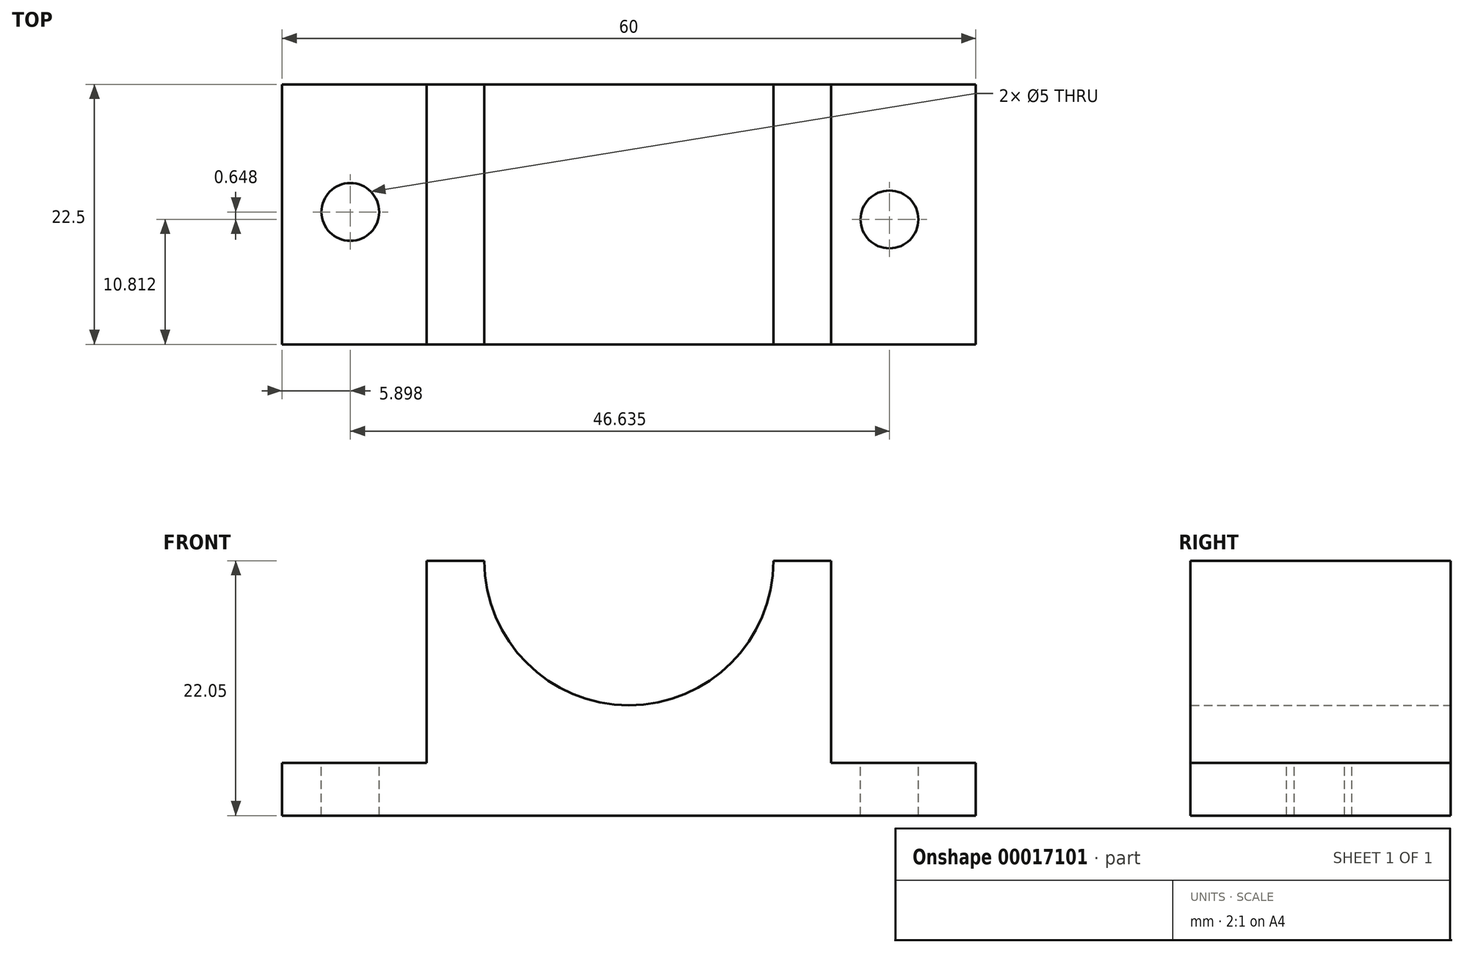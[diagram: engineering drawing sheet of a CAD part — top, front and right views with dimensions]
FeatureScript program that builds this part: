
annotation { "Feature Type Name" : "Feature", "Feature Type Description" : "" }
export const myFeature = defineFeature(function(context is Context, id is Id, definition is map)
    precondition{}
    {
        {
            var Q0;
            Q0=qCreatedBy(makeId("Front.planeOp"),FACE);
            var sketch = newSketch(context, id + "F0", { "sketchPlane" : qUnion([Q0])});
            skLineSegment(sketch, "E0", {"start": v(-1.56, 17.5) * mm, "end": v(-6.56, 17.5) * mm});
            skLineSegment(sketch, "E1", {"start": v(-6.56, 17.5) * mm, "end": v(-6.56, 0) * mm});
            skLineSegment(sketch, "E2", {"start": v(-6.56, 0) * mm, "end": v(-19.06, 0) * mm});
            skLineSegment(sketch, "E3", {"start": v(-19.06, 0) * mm, "end": v(-19.06, -4.55) * mm});
            skLineSegment(sketch, "E4", {"start": v(-19.06, -4.55) * mm, "end": v(40.94, -4.55) * mm});
            skLineSegment(sketch, "E5", {"start": v(40.94, -4.55) * mm, "end": v(40.94, 0) * mm});
            skLineSegment(sketch, "E6", {"start": v(40.94, 0) * mm, "end": v(28.44, 0) * mm});
            skLineSegment(sketch, "E7", {"start": v(28.44, 0) * mm, "end": v(28.44, 17.5) * mm});
            skLineSegment(sketch, "E8", {"start": v(28.44, 17.5) * mm, "end": v(23.44, 17.5) * mm});
            skArc(sketch, "E9", {"start": v(-1.56, 17.5) * mm, "mid": v(10.94, 5) * mm, "end": v(23.44, 17.5) * mm});
            skSolve(sketch);
        }
        {
            var Q0;
            Q0=makeQuery(id+"F0.imprint","IMPRINT",FACE,{"disambiguationData":[TD([[makeQuery(id+"F0.imprint","IMPRINT",EDGE,{"derivedFrom":sQuery(id+"F0.wireOp",EDGE,"E0")}),1.0]])]});
            extrude(context, id + "F1", {"entities" : qUnion([Q0]), "depth" : 22.5 * mm});
        }
        {
            var Q0;
            Q0=qCreatedBy(makeId("Top.planeOp"),FACE);
            var sketch = newSketch(context, id + "F2", { "sketchPlane" : qUnion([Q0])});
            skCircle(sketch, "E10", {"center": v(-13.16, -11.04) * mm, "radius": 2.5 * mm});
            skSolve(sketch);
        }
        {
            var Q0;
            Q0=qCreatedBy(makeId("Top.planeOp"),FACE);
            var sketch = newSketch(context, id + "F3", { "sketchPlane" : qUnion([Q0])});
            skCircle(sketch, "E11", {"center": v(33.47, -11.69) * mm, "radius": 2.5 * mm});
            skSolve(sketch);
        }
        {
            var Q0;
            Q0=sQuery(id+"F3.wireOp",VERTEX,"E11.center");
            var Q1;
            Q1=makeQuery(id+"F1.opExtrude","SWEPT_BODY",BODY,{"disambiguationData":[OSD([sQuery(id+"F0.wireOp",EDGE,"E0"),sQuery(id+"F0.wireOp",EDGE,"E1"),sQuery(id+"F0.wireOp",EDGE,"E2"),sQuery(id+"F0.wireOp",EDGE,"E3"),sQuery(id+"F0.wireOp",EDGE,"E4"),sQuery(id+"F0.wireOp",EDGE,"E5"),sQuery(id+"F0.wireOp",EDGE,"E6"),sQuery(id+"F0.wireOp",EDGE,"E7"),sQuery(id+"F0.wireOp",EDGE,"E8"),sQuery(id+"F0.wireOp",EDGE,"E9")])]});
            hole(context, id + "F4", {"style" : HoleStyle.SIMPLE, "holeDiameter" : 5 * mm, "endStyle" : HoleEndStyle.THROUGH, "locations" : qUnion([Q0]), "scope" : qUnion([Q1])});
        }
        {
            var Q0;
            Q0=sQuery(id+"F2.wireOp",VERTEX,"E10.center");
            var Q1;
            Q1=makeQuery(id+"F1.opExtrude","SWEPT_BODY",BODY,{"disambiguationData":[OSD([sQuery(id+"F0.wireOp",EDGE,"E0"),sQuery(id+"F0.wireOp",EDGE,"E1"),sQuery(id+"F0.wireOp",EDGE,"E2"),sQuery(id+"F0.wireOp",EDGE,"E3"),sQuery(id+"F0.wireOp",EDGE,"E4"),sQuery(id+"F0.wireOp",EDGE,"E5"),sQuery(id+"F0.wireOp",EDGE,"E6"),sQuery(id+"F0.wireOp",EDGE,"E7"),sQuery(id+"F0.wireOp",EDGE,"E8"),sQuery(id+"F0.wireOp",EDGE,"E9")])]});
            hole(context, id + "F5", {"style" : HoleStyle.SIMPLE, "holeDiameter" : 5 * mm, "endStyle" : HoleEndStyle.THROUGH, "locations" : qUnion([Q0]), "scope" : qUnion([Q1])});
        }
    });
